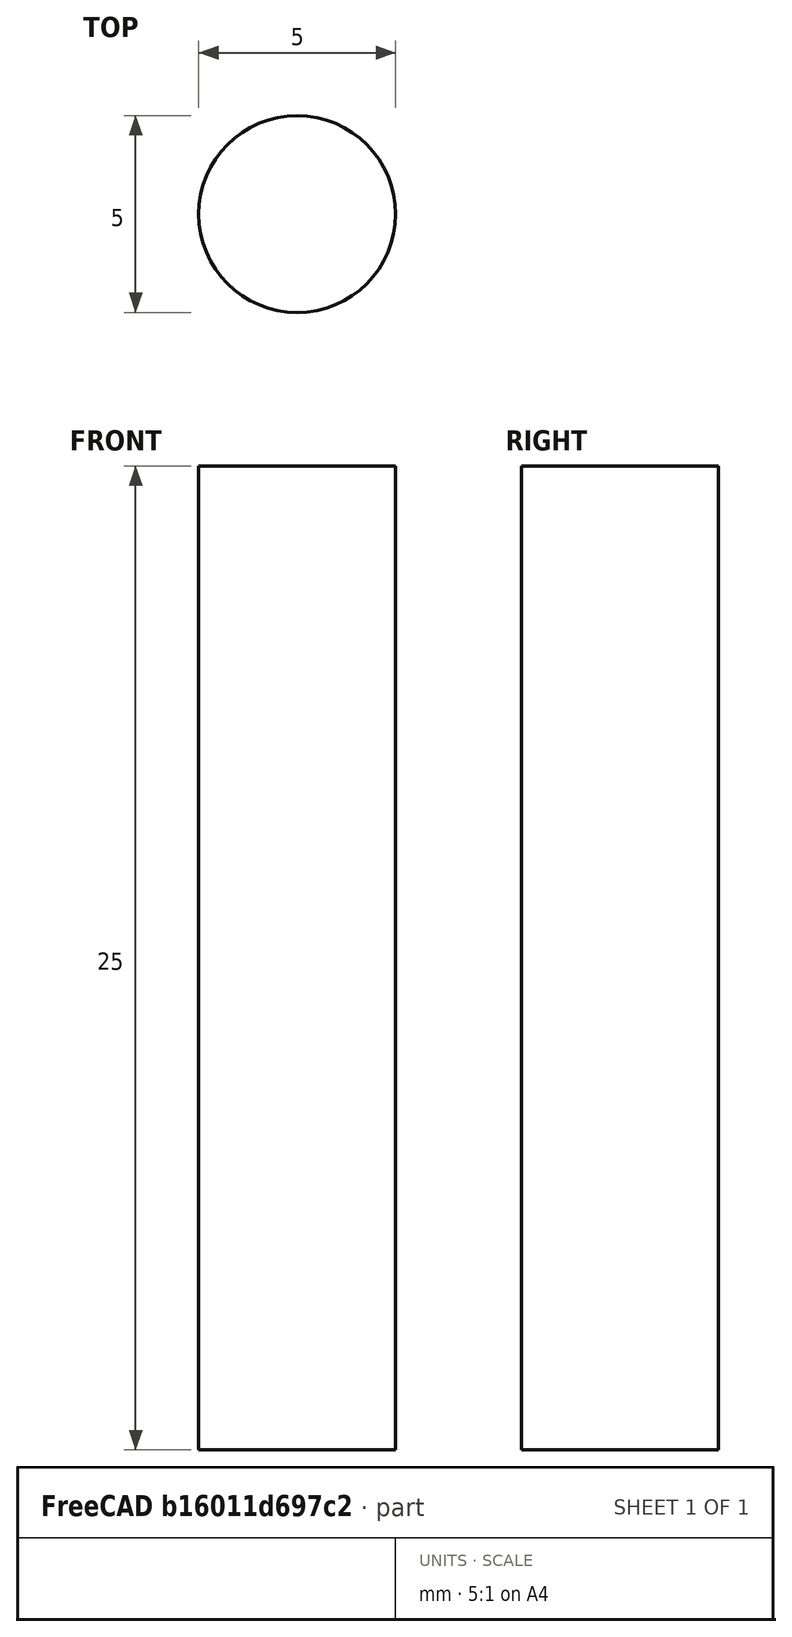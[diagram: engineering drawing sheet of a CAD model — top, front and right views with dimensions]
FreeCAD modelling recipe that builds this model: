
FCSTD DOCUMENT  (FreeCAD 1.0R39319 (Git))
Label: assognment1airpod_left
License: All rights reserved
LicenseURL: https://en.wikipedia.org/wiki/All_rights_reserved
objects: Part::FeaturePython×7, Sketcher::SketchObject×6, Part::Part2DObjectPython×2, Part::Loft×2, Part::Extrusion×2, Part::MultiFuse×2, Part::Mirroring×1, Part::Revolution×1, Part::MultiCommon×1, PartDesign::SubShapeBinder×1, App::DocumentObjectGroup×1
note: 31 computed .brp shape members not serialized (recipe doc carries the construction recipe); baked Part::Feature solids carry a one-line shape summary decoded from their .brp

FEATURE [Sketcher::SketchObject] Sketch  label="Front Profile"
  ArcFitTolerance = 1e-06
  FullyConstrained = true
  MakeInternals = false
  Placement = pos=(0,0,0) rot=(1,0,0;1.5708rad)
  sketch-geometry (9):
    g0-g4: Circle [constr] x5 (B-spline internal-alignment scaffolding for g5; pole/knot coordinates omitted)
    g5: BSplineCurve PolesCount=5 KnotsCount=3 Degree=3 IsPeriodic=0
    g6: GeomPoint [constr] X=-2 Y=0 Z=0
    g7: GeomPoint [constr] X=0 Y=3.5 Z=0
    g8: GeomPoint [constr] X=2 Y=0 Z=0
  constraints (15):
    c: Weight(g0) = 1
    c: Equal(g0, g1-g4) x4
    c: InternalAlignment(g0-g4 -> g5) x5
    c: InternalAlignment(g6,g5)
    c: InternalAlignment(g7,g5)
    c: InternalAlignment(g8,g5)
    c: PointOnObject(g0,g-1)
    c: PointOnObject(g4,g-1)
    c: Horizontal(g1,g3)
    c: Vertical(g1,g5)
    c: Vertical(g3,g5)
    c: DistanceX(g1,g3) = 4
    c: DistanceY(g-1,g1) = 3.5
    c: PointOnObject(g2,g-2)
    c: Coincident(g7,g2)
FEATURE [Sketcher::SketchObject] Sketch001  label="Mid_profile"
  ArcFitTolerance = 1e-06
  FullyConstrained = true
  MakeInternals = false
  Placement = pos=(0,8,0) rot=(1,0,0;1.5708rad)
  sketch-geometry (5):
    g0: ArcOfEllipse CenterX=0 CenterY=0 CenterZ=0 NormalX=0 NormalY=0 NormalZ=1 MajorRadius=7.5 MinorRadius=5 AngleXU=1.5708 StartAngle=4.71239 EndAngle=7.85398
    g1: LineSegment [constr] StartX=0 StartY=7.5 StartZ=0 EndX=0 EndY=-7.5 EndZ=0
    g2: LineSegment [constr] StartX=-5 StartY=0 StartZ=0 EndX=5 EndY=0 EndZ=0
    g3: GeomPoint [constr] X=0 Y=5.59017 Z=0
    g4: GeomPoint [constr] X=0 Y=-5.59017 Z=0
  constraints (7):
    c: InternalAlignment(g1-g4 -> g0) x4
    c: Coincident(g0,g-1)
    c: PointOnObject(g0,g2)
    c: DistanceX(g0,g0) = 10
    c: DistanceY(g-1,g1) = 7.5
    c: Horizontal(g2)
    c: PointOnObject(g0,g2)
FEATURE [Part::Part2DObjectPython] Clone2D  label="End_profile"  # Draft 2D object (typed FeaturePython)
  Fuse = false
  Objects = -> [Sketch001]
  Placement = pos=(0,10,0) rot=(1,0,0;1.5708rad)
  Scale = (1,1,1)
FEATURE [Part::Loft] Loft
  Closed = false
  MaxDegree = 5
  Ruled = false
  Sections = -> [Sketch,Sketch001,Clone2D]
  Solid = false
FEATURE [Part::Mirroring] Part__Mirroring  label="Loft (Mirror #1)"
  Base = (0,0,0)
  Normal = (0,0,1)
  Source = -> Loft
FEATURE [Sketcher::SketchObject] Sketch002  label="refline"
  ArcFitTolerance = 1e-06
  ExternalGeometry = -> [Clone2D,Part__Mirroring]
  FullyConstrained = true
  MakeInternals = false
  sketch-geometry (1):
    g0: LineSegment StartX=-5 StartY=10 StartZ=0 EndX=5 EndY=10 EndZ=0
  constraints (2):
    c: Coincident(g0,g-3)
    c: Coincident(g0,g-4)
FEATURE [Part::Revolution] Revolve
  Angle = -180
  Axis = (1,0,0)
  AxisLink = -> Sketch002 [Edge1]
  Base = (5,10,0)
  FaceMakerClass = Part::FaceMakerBullseye
  Solid = false
  Source = -> Clone2D
  Symmetric = false
FEATURE [Sketcher::SketchObject] Sketch003
  ArcFitTolerance = 1e-06
  FullyConstrained = false
  MakeInternals = false
  sketch-geometry (9):
    g0-g4: Circle [constr] x5 (B-spline internal-alignment scaffolding for g5; pole/knot coordinates omitted)
    g5: BSplineCurve PolesCount=5 KnotsCount=3 Degree=3 IsPeriodic=0
    g6: GeomPoint [constr] X=1.80743 Y=17.7931 Z=0
    g7: GeomPoint [constr] X=3.08465 Y=3.84068 Z=0
    g8: GeomPoint [constr] X=5.42892 Y=0.591039 Z=0
  constraints (6):
    c: Weight(g0) = 1
    c: Equal(g0, g1-g4) x4
    c: InternalAlignment(g0-g4 -> g5) x5
    c: InternalAlignment(g6,g5)
    c: InternalAlignment(g7,g5)
    c: InternalAlignment(g8,g5)
FEATURE [Part::Extrusion] Extrude
  Base = -> Sketch003
  Dir = (0,0,1)
  DirMode = 2
  FaceMakerClass = Part::FaceMakerBullseye
  FaceMakerMode = 3
  LengthFwd = 20
  LengthRev = 0
  Solid = false
  Symmetric = true
FEATURE [Part::MultiCommon] Common
  Refine = true
  Shapes = -> [Loft]
FEATURE [Part::MultiFuse] Fusion
  Refine = true
  Shapes = -> [Common,Part__Mirroring,Revolve]
FEATURE [Part::FeaturePython] Slice  # WARN: FeaturePython — macro-defined, semantics opaque (R4)
  Base = -> Fusion
  Mode = 1
  Tolerance = 0
  Tools = -> [Extrude]
FEATURE [Part::FeaturePython] Slice_child0  label="Slice.006"  # WARN: FeaturePython — macro-defined, semantics opaque (R4)
  Base = -> Slice
  FilterType = 1
  Invert = false
  OverrideMaxVal = 0
  WindowFrom = 80
  WindowTo = 100
  items = 0
FEATURE [Part::FeaturePython] Slice_child1  label="Slice.007"  # WARN: FeaturePython — macro-defined, semantics opaque (R4)
  Base = -> Slice
  FilterType = 1
  Invert = false
  OverrideMaxVal = 0
  WindowFrom = 80
  WindowTo = 100
  items = 1
FEATURE [Part::FeaturePython] Slice_child2  label="slice3"  # WARN: FeaturePython — macro-defined, semantics opaque (R4)
  Base = -> Slice
  FilterType = 1
  Invert = false
  OverrideMaxVal = 0
  WindowFrom = 80
  WindowTo = 100
  items = 2
FEATURE [Part::FeaturePython] Slice_child3  label="Slice.3"  # WARN: FeaturePython — macro-defined, semantics opaque (R4)
  Base = -> Slice
  FilterType = 1
  Invert = false
  OverrideMaxVal = 0
  WindowFrom = 80
  WindowTo = 100
  items = 3
FEATURE [Part::FeaturePython] Slice_child4  label="Slice.4"  # WARN: FeaturePython — macro-defined, semantics opaque (R4)
  Base = -> Slice
  FilterType = 1
  Invert = false
  OverrideMaxVal = 0
  WindowFrom = 80
  WindowTo = 100
  items = 4
FEATURE [Part::FeaturePython] Slice_child5  label="Slice.008"  # WARN: FeaturePython — macro-defined, semantics opaque (R4)
  Base = -> Slice
  FilterType = 1
  Invert = false
  OverrideMaxVal = 0
  WindowFrom = 80
  WindowTo = 100
  items = 5
FEATURE [Sketcher::SketchObject] Sketch004
  ArcFitTolerance = 1e-06
  AttachmentSupport = -> [Slice_child4]
  FullyConstrained = true
  MakeInternals = false
  MapMode = 45
  Placement = pos=(3.54146,13.1422,5.00444e-09) rot=(0.463452,0.626583,0.626583;2.27362rad)
FEATURE [Sketcher::SketchObject] Sketch005
  ArcFitTolerance = 1e-06
  FullyConstrained = true
  MakeInternals = false
  Placement = pos=(0,0,-5) rot=(0,0,1;0rad)
  sketch-geometry (1):
    g0: Circle CenterX=10 CenterY=12 CenterZ=0 NormalX=0 NormalY=0 NormalZ=1 AngleXU=0 Radius=2.5
  constraints (3):
    c: Diameter(g0) = 5
    c: Distance(g0,g-1) = 12
    c: Distance(g0,g-2) = 10
FEATURE [Part::Extrusion] Extrude002
  Base = -> Sketch005
  Dir = (0,0,1)
  DirMode = 2
  FaceMakerClass = Part::FaceMakerBullseye
  FaceMakerMode = 3
  LengthFwd = -25
  LengthRev = 0
  Solid = true
  Symmetric = false
FEATURE [PartDesign::SubShapeBinder] Binder
  BindCopyOnChange = 0
  BindMode = 0
  ClaimChildren = false
  Fuse = false
  MakeFace = true
  OffsetFill = false
  OffsetIntersection = false
  OffsetJoinType = 0
  OffsetOpenResult = false
  PartialLoad = false
  Refine = true
  Relative = true
  Support = -> [Slice_child2[Edge3],Slice_child5[Edge4],Slice_child0[Edge3]]
  _Version = 2
FEATURE [Part::Part2DObjectPython] Clone2D001  label="Sketch005 (2D)"  # Draft 2D object (typed FeaturePython)
  Fuse = false
  Objects = -> [Sketch005]
  Placement = pos=(0,0,-5) rot=(0,1,0;5.95157rad)
  Scale = (1,1,1)
FEATURE [Part::Loft] Loft001
  Closed = false
  MaxDegree = 5
  Ruled = false
  Sections = -> [Sketch005,Clone2D001,Binder]
  Solid = false
FEATURE [Part::MultiFuse] Fusion001
  Refine = true
  Shapes = -> [Loft001,Slice_child3,Slice_child4]
FEATURE [App::DocumentObjectGroup] GrExplode_Slice  label="ExplodedSlice"
  Group = -> [Slice_child0,Slice_child1,Slice_child2,Slice_child5,Sketch004,Fusion001]
